# Revit family: Grab_Bar-Wall_Floor-Bobrick-819298_Series
name_source: partatom
category: Specialty Equipment
units: mm (PartAtom-declared; Revit-internal decimal feet)

## family parameters
Cut with Voids When Loaded = No
Host = Face
OmniClass Number = 23.40.20.21.47
OmniClass Title = Bath Grab Bars
Part Type = Normal
Room Calculation Point = No
Round Connector Dimension = Use Diameter
Shared = Yes

## types (1)
- 819298
    Assembly Code = E2010
    Bar Diameter = 1 1/2"
    Default Elevation = 0"
    Description = 1½" (38mm) DIAMETERSTAINLESS STEELDRINKING FOUNTAINGRAB BAR
    Finish = Stainless Steel-Bobrick-Type 304-Satin
    Height = 33"
    IAPMO Compliance = Grab bar shall comply with barrier-free accessibility guidelines (including ADAAG in the U.S.A.) for structural strength.
    Installation Type = Surface Mounted
    Length = 30"
    Manufacturer = Bobrick
    Material = Stainless Steel-Bobrick-Type 304-Satin
    Model = 819298
    Price = Prices may vary. Please consult Manufacturer Representative for most up-to-date price list.
    Snap Flange Cover Diameter = 3 1/4"
    URL = https://www.bobrick.com
    Width = 3 3/16"

## geometry (parser evidence)
native form markers: Sweep x3
no freeform markers — native parametric forms only
